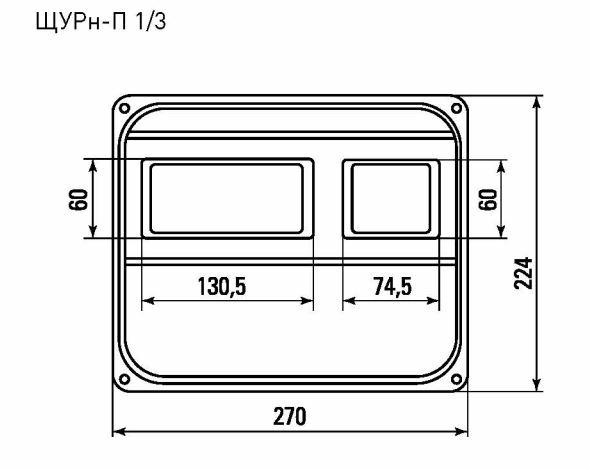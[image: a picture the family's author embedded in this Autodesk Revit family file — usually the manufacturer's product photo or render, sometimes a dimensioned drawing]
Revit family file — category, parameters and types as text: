
# Revit family: EKF_EE_ЩУ_IP54_Basic
name_source: partatom
category: Электрооборудование
units: mm (PartAtom-declared; Revit-internal decimal feet)

## family parameters
Всегда вертикально = Да
На основе рабочей плоскости = Нет
Общий = Нет
При загрузке вырезать с полостями = Нет
Размер круглого соединителя = Использовать диаметр
Тип детали = Силовой щит
Точка расчета площади = Да

## types (5) — shared parameters
ADSK_Единица измерения = компл.
ADSK_Завод-изготовитель = EKF
ADSK_Классификация нагрузок = Прочее
ADSK_Количество = 1
ADSK_Коэффициент мощности = 1
ADSK_Материал = RAL 7035_Сталь
ADSK_Напряжение = 400 В
ADSK_Номинальная мощность = 0 Вт
ADSK_Полная мощность = 0 В·А
ADSK_Ток = 125 А
Изготовитель = EKF
Серия номенклатуры = Basic
Степень защиты IP = IP54
ТВ = EKF
Тип установки = Навесной
zero-valued in all types: Количество DIN-реек, Количество модулей на DIN-рейке, Максимальное количество модулей

## per-type parameters (varying)
| type | ADSK_Код изделия | ADSK_Количество фаз | ADSK_Марка | ADSK_Масса | ADSK_Наименование | ADSK_Обозначение | ADSK_Размер_Высота | ADSK_Размер_Глубина | ADSK_Размер_Ширина | Описание | Тип |
| ЩУ-1/1-0 (310х300х150) IP54 EKF Basic | mb54-1-bas | 1 | ЩУ-1/1-0 IP54 | 4.78 | Щит учетный ЩУ-1/1-0 (310х300х150) IP54 EKF Basic | ЩУ-1/1-0 IP54 | 310 мм | 150 мм | 300 мм | Щит учетный ЩУ-1/1-0 (310х300х150) IP54 EKF Basic | 55 мм |
| ЩУ-1/1-0 для счетчика на дин-рейку (250х300х100) IP54 EKF Basic | mb54-1E-bas | 1 | ЩУ-1/1-0 для счетчика на дин-рейку IP54 | 2.2 | Щит учетный ЩУ-1/1-0 для счетчика на дин-рейку (250х300х100) IP54 EKF Basic | ЩУ-1/1-0 для счетчика на дин-рейку IP54 | 250 мм | 100 мм | 300 мм | Щит учетный ЩУ-1/1-0 для счетчика на дин-рейку (250х300х100) IP54 EKF Basic | 56 мм |
| ЩУ-1/1-1 двухдверный (310х300х160) IP54 EKF Basic | mb54-1-2-bas | 1 | ЩУ-1/1-1 двухдверный IP54 | 5.23 | Щит учетный ЩУ-1/1-1 двухдверный (310х300х160) IP54 EKF Basic | ЩУ-1/1-1 двухдверный IP54 | 310 мм | 160 мм | 300 мм | Щит учетный ЩУ-1/1-1 двухдверный (310х300х160) IP54 EKF Basic | 57 мм |
| ЩУ-3/1-0 (ЩУРН-3/12) (540х310х165) 12 мод. IP54 EKF Basic | mb54-3-bas | 3 | ЩУ-3/1-0 (ЩУРН-3/12) 12 мод. IP54 | 5.3 | Щит учетный ЩУ-3/1-0 (ЩУРН-3/12) (540х310х165) 12 мод. IP54 EKF Basic | ЩУ-3/1-0 (ЩУРН-3/12) 12 мод. IP54 | 540 мм | 165 мм | 310 мм | Щит учетный ЩУ-3/1-0 (ЩУРН-3/12) (540х310х165) 12 мод. IP54 EKF Basic | 58 мм |
| ЩУ-3/1-1 двухдверный (445х400х150) 12 мод. IP54 EKF Basic | mb54-3-2-bas | 3 | ЩУ-3/1-1 двухдверный 12 мод. IP54 | 7.55 | Щит учетный ЩУ-3/1-1 двухдверный (445х400х150) 12 мод. IP54 EKF Basic | ЩУ-3/1-1 двухдверный 12 мод. IP54 | 445 мм | 150 мм | 400 мм | Щит учетный ЩУ-3/1-1 двухдверный (445х400х150) 12 мод. IP54 EKF Basic | 59 мм |
